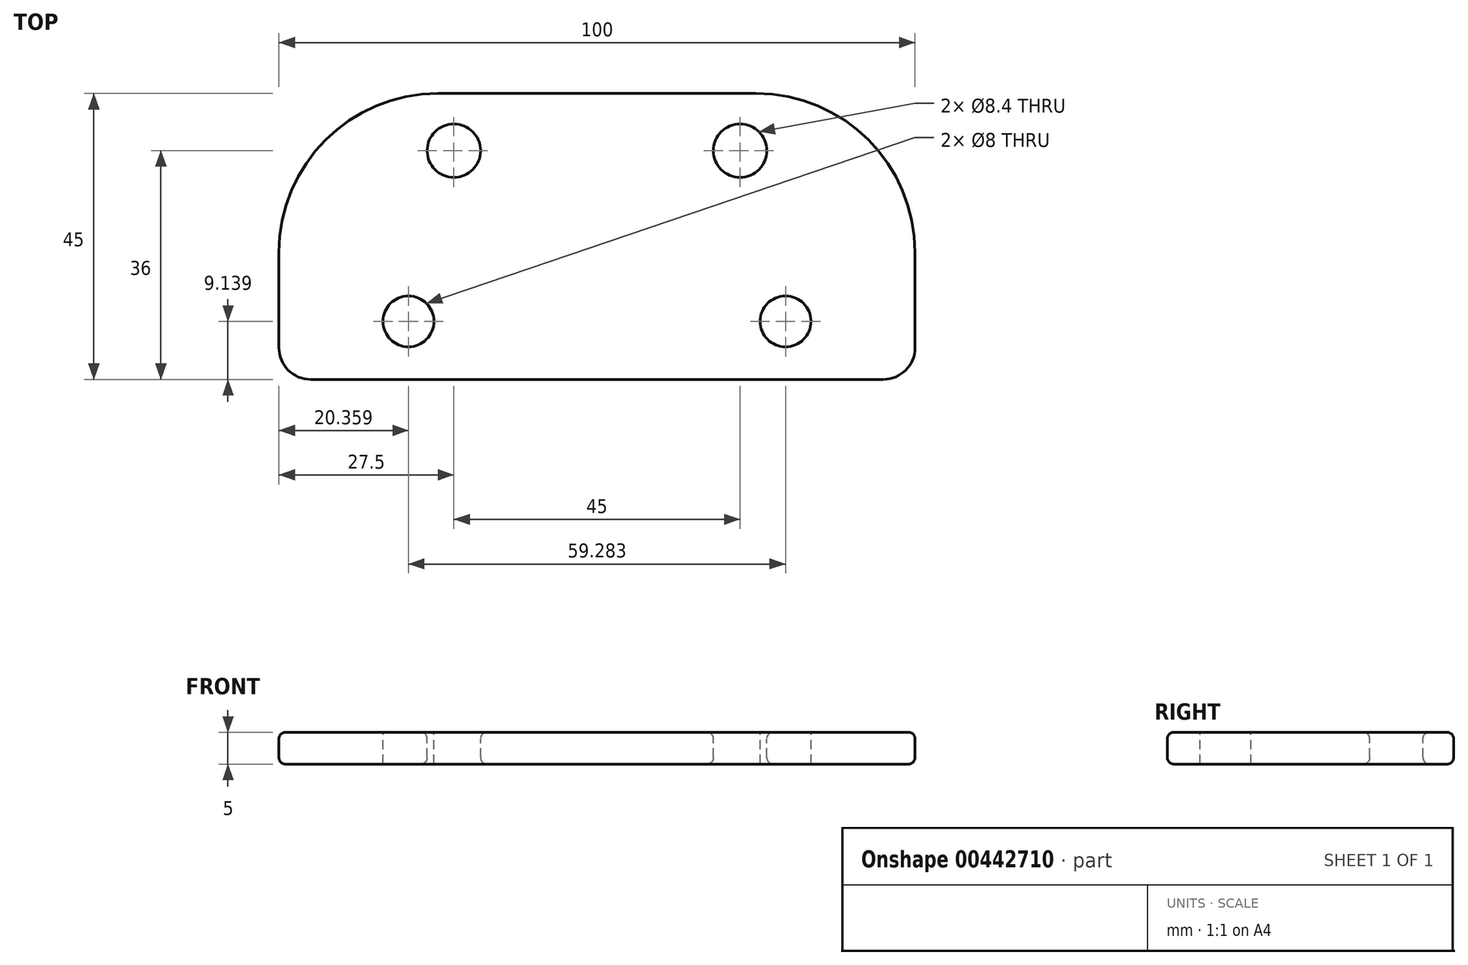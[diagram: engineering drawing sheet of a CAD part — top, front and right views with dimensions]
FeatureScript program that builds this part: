
annotation { "Feature Type Name" : "Feature", "Feature Type Description" : "" }
export const myFeature = defineFeature(function(context is Context, id is Id, definition is map)
    precondition{}
    {
        {
            var Q0;
            Q0=qCreatedBy(makeId("Top.planeOp"),FACE);
            var sketch = newSketch(context, id + "F0", { "sketchPlane" : qUnion([Q0])});
            skLineSegment(sketch, "E0.bottom", {"start": v(-25, 22.5) * mm, "end": v(25, 22.5) * mm});
            skLineSegment(sketch, "E0.top", {"start": v(-50, -22.5) * mm, "end": v(50, -22.5) * mm});
            skLineSegment(sketch, "E0.left", {"start": v(-50, -2.5) * mm, "end": v(-50, -22.5) * mm});
            skLineSegment(sketch, "E0.right", {"start": v(50, -2.5) * mm, "end": v(50, -22.5) * mm});
            skPoint(sketch, "E0.middle", {"position": v(0, 0) * mm});
            skCircle(sketch, "E1", {"center": v(22.5, 13.5) * mm, "radius": 25 * mm, "construction": true});
            skLineSegment(sketch, "E2", {"start": v(0, -2.6) * mm, "end": v(0, 84.85) * mm, "construction": true});
            skCircle(sketch, "E3.MirrorC", {"center": v(-22.5, 13.5) * mm, "radius": 25 * mm, "construction": true});
            skCircle(sketch, "E4", {"center": v(-22.5, 13.5) * mm, "radius": 4.2 * mm});
            skCircle(sketch, "E5.MirrorC", {"center": v(22.5, 13.5) * mm, "radius": 4.2 * mm});
            skPoint(sketch, "E6.visualSharp", {"position": v(-50, 22.5) * mm});
            skArc(sketch, "E6.filletArc", {"start": v(-25, 22.5) * mm, "mid": v(-42.68, 15.18) * mm, "end": v(-50, -2.5) * mm});
            skPoint(sketch, "E7.visualSharp", {"position": v(50, 22.5) * mm});
            skArc(sketch, "E7.filletArc", {"start": v(50, -2.5) * mm, "mid": v(42.68, 15.18) * mm, "end": v(25, 22.5) * mm});
            skSolve(sketch);
        }
        {
            var Q0;
            Q0 = qSketchRegion(id + "F0", true);
            extrude(context, id + "F1", {"entities" : qUnion([Q0]), "oppositeDirection" : true, "depth" : 5 * mm});
        }
        {
            var Q0;
            Q0=makeQuery(id+"F1.opExtrude","SWEPT_EDGE",EDGE,{"disambiguationData":[OSD([sQuery(id+"F0.wireOp",EDGE,"E0.top"),sQuery(id+"F0.wireOp",EDGE,"E0.right")])]});
            var Q1;
            Q1=makeQuery(id+"F1.opExtrude","SWEPT_EDGE",EDGE,{"disambiguationData":[OSD([sQuery(id+"F0.wireOp",EDGE,"E0.top"),sQuery(id+"F0.wireOp",EDGE,"E0.left")])]});
            fillet(context, id + "F2", {"entities" : qUnion([Q0, Q1]), "radius" : 5 * mm, "tangentPropagation" : true, "allowEdgeOverflow" : false});
        }
        {
            var Q0;
            Q0=makeQuery(id+"F1.opExtrude","CAP_FACE",FACE,{"disambiguationData":[OSD([sQuery(id+"F0.wireOp",EDGE,"E0.bottom"),sQuery(id+"F0.wireOp",EDGE,"E0.top"),sQuery(id+"F0.wireOp",EDGE,"E0.left"),sQuery(id+"F0.wireOp",EDGE,"E0.right"),sQuery(id+"F0.wireOp",EDGE,"E4"),sQuery(id+"F0.wireOp",EDGE,"E5.MirrorC"),sQuery(id+"F0.wireOp",EDGE,"E6.filletArc"),sQuery(id+"F0.wireOp",EDGE,"E7.filletArc")])],"isStart":true});
            var Q1;
            Q1=makeQuery(id+"F1.opExtrude","CAP_FACE",FACE,{"disambiguationData":[OSD([sQuery(id+"F0.wireOp",EDGE,"E0.bottom"),sQuery(id+"F0.wireOp",EDGE,"E0.top"),sQuery(id+"F0.wireOp",EDGE,"E0.left"),sQuery(id+"F0.wireOp",EDGE,"E0.right"),sQuery(id+"F0.wireOp",EDGE,"E4"),sQuery(id+"F0.wireOp",EDGE,"E5.MirrorC"),sQuery(id+"F0.wireOp",EDGE,"E6.filletArc"),sQuery(id+"F0.wireOp",EDGE,"E7.filletArc")])],"isStart":false});
            fillet(context, id + "F3", {"entities" : qUnion([Q0, Q1]), "radius" : 1 * mm, "tangentPropagation" : true, "allowEdgeOverflow" : false});
        }
        {
            var Q0;
            Q0=makeQuery(id+"F1.opExtrude","CAP_FACE",FACE,{"disambiguationData":[OSD([sQuery(id+"F0.wireOp",EDGE,"E0.bottom"),sQuery(id+"F0.wireOp",EDGE,"E0.top"),sQuery(id+"F0.wireOp",EDGE,"E0.left"),sQuery(id+"F0.wireOp",EDGE,"E0.right"),sQuery(id+"F0.wireOp",EDGE,"E4"),sQuery(id+"F0.wireOp",EDGE,"E5.MirrorC"),sQuery(id+"F0.wireOp",EDGE,"E6.filletArc"),sQuery(id+"F0.wireOp",EDGE,"E7.filletArc")])],"isStart":true});
            var sketch = newSketch(context, id + "F4", { "sketchPlane" : qUnion([Q0])});
            skCircle(sketch, "E8", {"center": v(29.64, -13.36) * mm, "radius": 4 * mm});
            skLineSegment(sketch, "E9", {"start": v(-1.39, 0) * mm, "end": v(-1.17, -1.75) * mm, "construction": true});
            skCircle(sketch, "E10.MirrorC", {"center": v(-29.64, -13.36) * mm, "radius": 4 * mm});
            skSolve(sketch);
        }
        {
            var Q0;
            Q0 = qSketchRegion(id + "F4", true);
            extrude(context, id + "F5", {"entities" : qUnion([Q0]), "operationType" : NewBodyOperationType.REMOVE, "endBound" : BoundingType.THROUGH_ALL, "oppositeDirection" : true, "depth" : 25 * mm});
        }
    });
